# Revit family: Faucet-Wall_Mount-Bath_Spout-KOHLER-Strayt-K-37344IN_1
name_source: partatom
category: Plumbing Fixtures
units: mm (PartAtom-declared; Revit-internal decimal feet)

## family parameters
Cut with Voids When Loaded = No
Host = Face
OmniClass Number = 23.31.11.00
OmniClass Title = Faucets
Part Type = Normal
Room Calculation Point = No
Round Connector Dimension = Use Diameter
Shared = No

## types (5) — shared parameters
ADA Compliant = No
Assembly Code = D2010
CW Connection = No
Cold Water Inlet = Cold Water Inlet
Date Modified = 03/08/2023
Default Elevation = 36"
Description = Wall Mount Bath Spout Without Diverter
Drain Included = No
Flow Rate = 0 GPM
HW Connection = Yes
Height = 1 13/16"
Length = 6 5/16"
Manufacturer = Kohler Co.
Master Format 2014 = 22 41 39
Master Format 2014 Name = Residential Faucets, Supplies, and Trim
Material = Premium Metal Construction
Pressure = 60.00 psi
Product Name = Strayt
Product Page URL = https://www.kohler.co.in
Spout Reach = 6 5/16"
Tempered Water Inlet = Tempered Water Inlet
URL = https://www.kohler.co.in
Vent Connection = No
Waste Connection = No
Waste Water Outlet = Waste Water Outlet
WaterSense Certified = No
Width = 2 1/2"

## per-type parameters (varying)
| type | Finish | Model | Type |
| AF-Vibrant French Gold | Kohler-Metal-AF-Vibrant_French_Gold | K-37344IN-AF | 1 |
| BN-Vibrant Brushed Nickel | Kohler-Metal-BN-Vibrant_Brushed_Nickel | K-37344IN-BN | 2 |
| BV-Brushed Bronze | Kohler-Metal-BV-Brushed_Bronze | K-37344IN-BV | 3 |
| CP-Polished Chrome | Kohler-Metal-CP-Polished_Chrome | K-37344IN-CP | 4 |
| RGD-Polished Rose Gold | Kohler-Metal-RGD-Polished_Rose_Gold | K-37344IN-RGD | 5 |

## geometry (parser evidence)
native form markers: Sweep x5
no freeform markers — native parametric forms only
